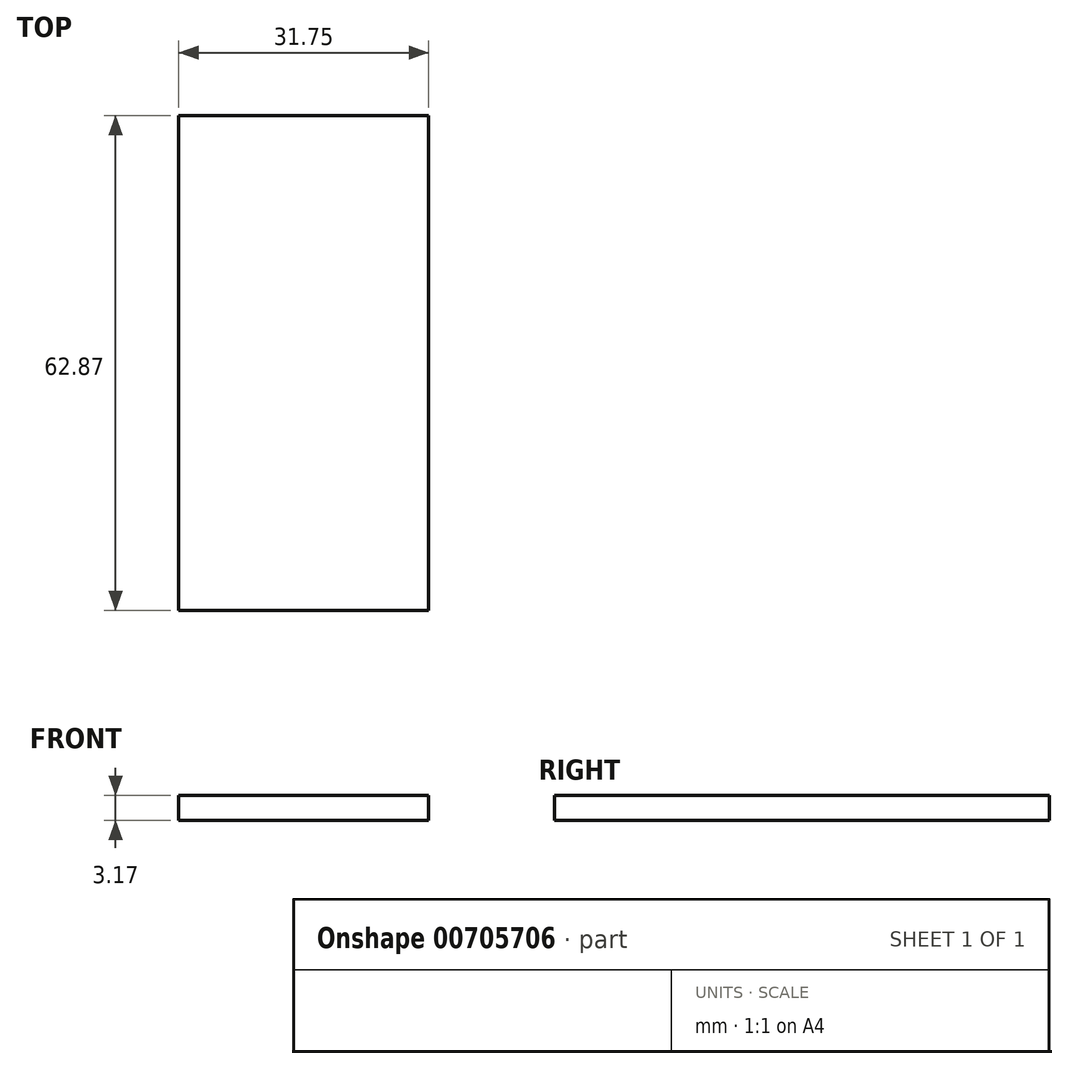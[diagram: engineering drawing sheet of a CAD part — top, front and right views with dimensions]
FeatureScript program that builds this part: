
annotation { "Feature Type Name" : "Feature", "Feature Type Description" : "" }
export const myFeature = defineFeature(function(context is Context, id is Id, definition is map)
    precondition{}
    {
        {
            var Q0;
            Q0=qCreatedBy(makeId("Top.planeOp"),FACE);
            var sketch = newSketch(context, id + "F0", { "sketchPlane" : qUnion([Q0])});
            skLineSegment(sketch, "E0.bottom", {"start": v(0, 0) * mm, "end": v(31.75, 0) * mm});
            skLineSegment(sketch, "E0.top", {"start": v(0, 62.87) * mm, "end": v(31.75, 62.87) * mm});
            skLineSegment(sketch, "E0.left", {"start": v(0, 0) * mm, "end": v(0, 62.87) * mm});
            skLineSegment(sketch, "E0.right", {"start": v(31.75, 0) * mm, "end": v(31.75, 62.87) * mm});
            skSolve(sketch);
        }
        {
            var Q0;
            Q0 = qSketchRegion(id + "F0", true);
            extrude(context, id + "F1", {"entities" : qUnion([Q0]), "depth" : 3.17 * mm, "offsetDistance" : 25.4 * mm});
        }
    });
